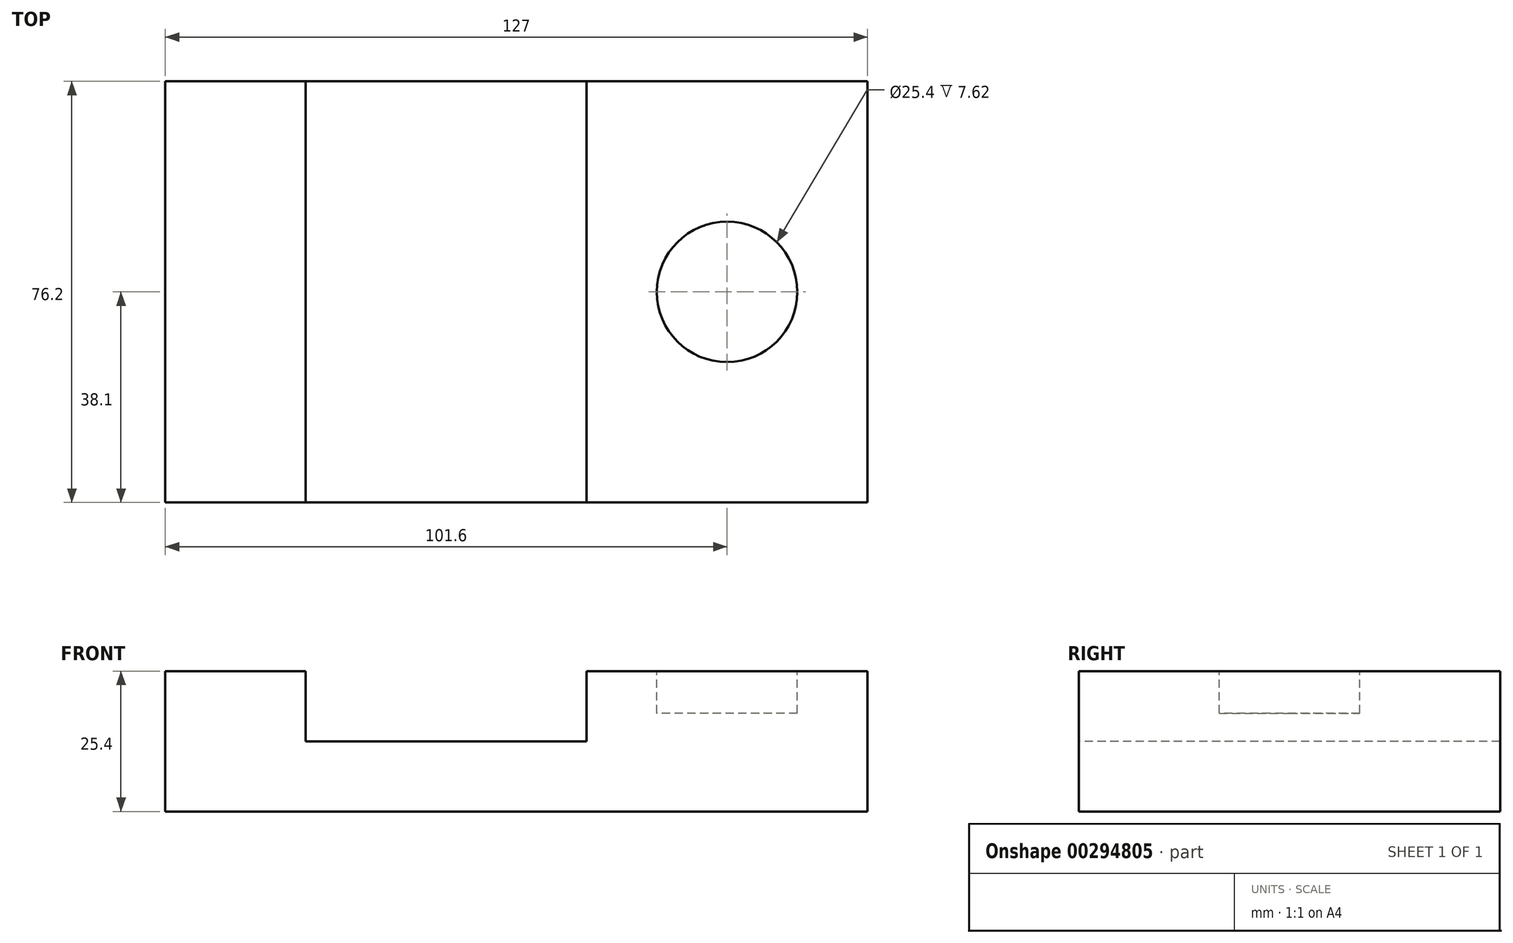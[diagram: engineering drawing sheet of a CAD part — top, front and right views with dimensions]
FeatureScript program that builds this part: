
annotation { "Feature Type Name" : "Feature", "Feature Type Description" : "" }
export const myFeature = defineFeature(function(context is Context, id is Id, definition is map)
    precondition{}
    {
        {
            var Q0;
            Q0=qCreatedBy(makeId("Top.planeOp"),FACE);
            var sketch = newSketch(context, id + "F0", { "sketchPlane" : qUnion([Q0])});
            skLineSegment(sketch, "E0.bottom", {"start": v(0, 0) * mm, "end": v(127, 0) * mm});
            skLineSegment(sketch, "E0.top", {"start": v(0, -76.2) * mm, "end": v(127, -76.2) * mm});
            skLineSegment(sketch, "E0.left", {"start": v(0, 0) * mm, "end": v(0, -76.2) * mm});
            skLineSegment(sketch, "E0.right", {"start": v(127, 0) * mm, "end": v(127, -76.2) * mm});
            skSolve(sketch);
        }
        {
            var Q0;
            Q0=makeQuery(id+"F0.imprint","IMPRINT",FACE,{"disambiguationData":[TD([[makeQuery(id+"F0.imprint","IMPRINT",EDGE,{"derivedFrom":sQuery(id+"F0.wireOp",EDGE,"E0.bottom")}),-1.0]])]});
            extrude(context, id + "F1", {"entities" : qUnion([Q0]), "depth" : 25.4 * mm});
        }
        {
            var Q0;
            Q0=makeQuery(id+"F1.opExtrude","CAP_FACE",FACE,{"disambiguationData":[OSD([sQuery(id+"F0.wireOp",EDGE,"E0.bottom"),sQuery(id+"F0.wireOp",EDGE,"E0.top"),sQuery(id+"F0.wireOp",EDGE,"E0.left"),sQuery(id+"F0.wireOp",EDGE,"E0.right")])],"isStart":false});
            var sketch = newSketch(context, id + "F2", { "sketchPlane" : qUnion([Q0])});
            skLineSegment(sketch, "E1.bottom", {"start": v(25.4, 0) * mm, "end": v(76.2, 0) * mm});
            skLineSegment(sketch, "E1.top", {"start": v(25.4, -76.2) * mm, "end": v(76.2, -76.2) * mm});
            skLineSegment(sketch, "E1.left", {"start": v(25.4, 0) * mm, "end": v(25.4, -76.2) * mm});
            skLineSegment(sketch, "E1.right", {"start": v(76.2, 0) * mm, "end": v(76.2, -76.2) * mm});
            skSolve(sketch);
        }
        {
            var Q0;
            Q0=makeQuery(id+"F2.imprint","IMPRINT",FACE,{"disambiguationData":[TD([[makeQuery(id+"F2.imprint","IMPRINT",EDGE,{"derivedFrom":sQuery(id+"F2.wireOp",EDGE,"E1.bottom")}),-1.0]])]});
            extrude(context, id + "F3", {"entities" : qUnion([Q0]), "operationType" : NewBodyOperationType.REMOVE, "oppositeDirection" : true, "depth" : 12.7 * mm});
        }
        {
            var Q0;
            {var subQ0=sQuery(id+"F0.wireOp",EDGE,"E0.bottom");var subQ1=sQuery(id+"F0.wireOp",EDGE,"E0.right");var subQ2=sQuery(id+"F0.wireOp",EDGE,"E0.top");Q0=makeQuery(id+"F3.boolean.opBoolean","SPLIT",FACE,{"disambiguationData":[TD([makeQuery(id+"F1.opExtrude","SWEPT_FACE",FACE,{"disambiguationData":[OSD([subQ1])]})])],"derivedFrom":makeQuery(id+"F1.opExtrude","CAP_FACE",FACE,{"disambiguationData":[OSD([subQ0,subQ2,sQuery(id+"F0.wireOp",EDGE,"E0.left"),subQ1])],"isStart":false})});}
            var sketch = newSketch(context, id + "F4", { "sketchPlane" : qUnion([Q0])});
            skCircle(sketch, "E2", {"center": v(101.6, -38.1) * mm, "radius": 12.7 * mm});
            skSolve(sketch);
        }
        {
            var Q0;
            Q0=makeQuery(id+"F4.imprint","IMPRINT",FACE,{"disambiguationData":[TD([[makeQuery(id+"F4.imprint","IMPRINT",EDGE,{"derivedFrom":sQuery(id+"F4.wireOp",EDGE,"E2")}),1.0]])]});
            extrude(context, id + "F5", {"entities" : qUnion([Q0]), "operationType" : NewBodyOperationType.REMOVE, "oppositeDirection" : true, "depth" : 7.62 * mm});
        }
    });
